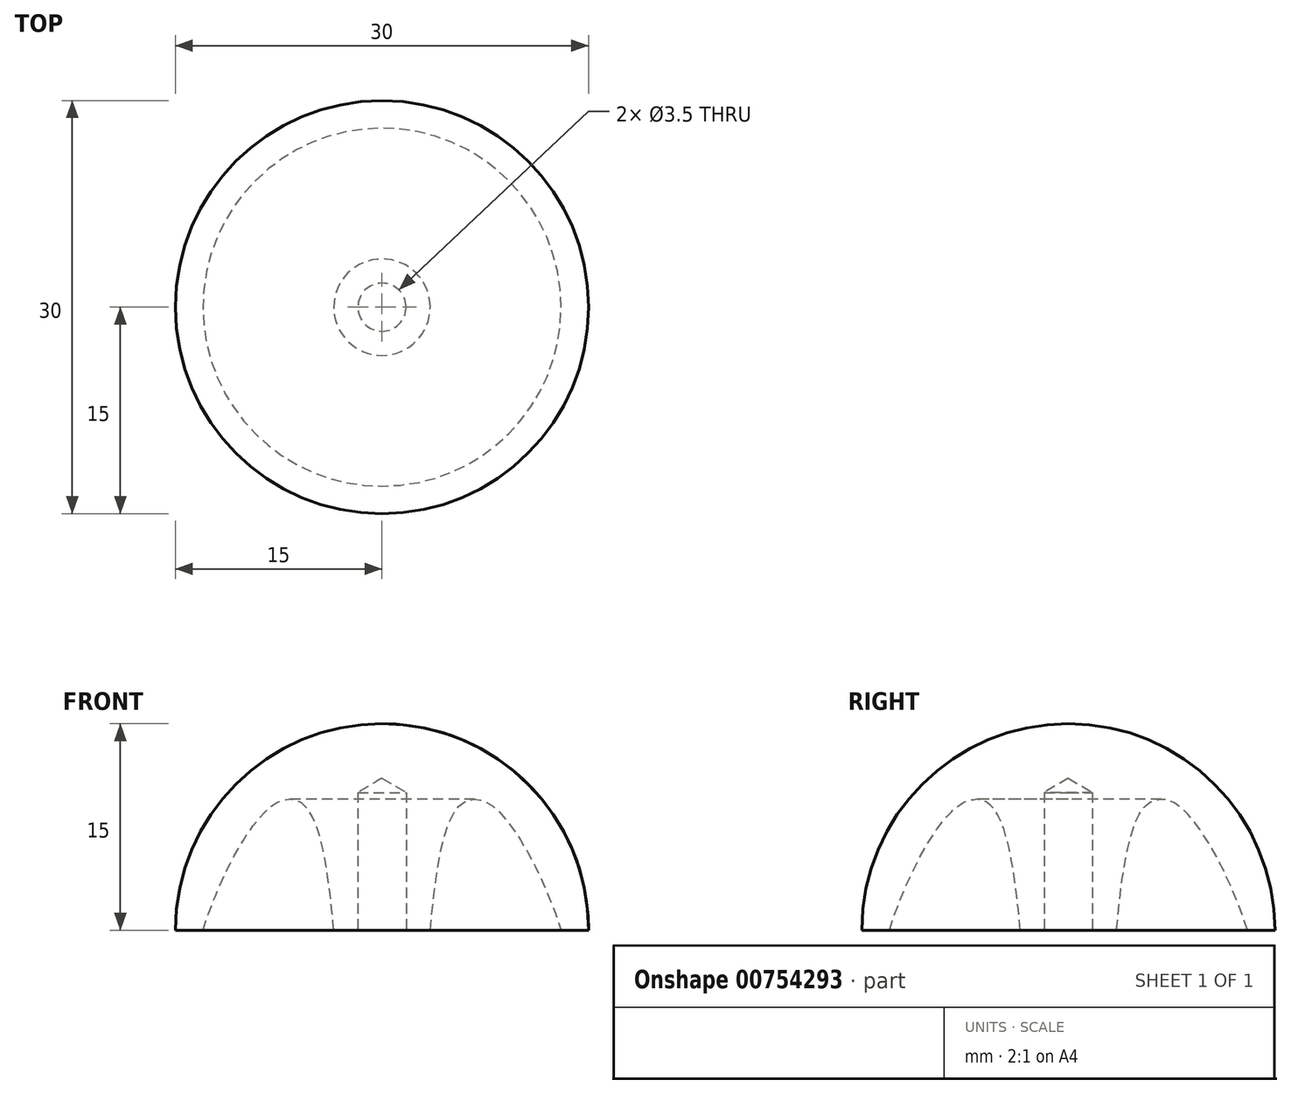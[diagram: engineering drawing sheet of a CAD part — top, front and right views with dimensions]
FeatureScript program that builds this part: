
annotation { "Feature Type Name" : "Feature", "Feature Type Description" : "" }
export const myFeature = defineFeature(function(context is Context, id is Id, definition is map)
    precondition{}
    {
        {
            var Q0;
            Q0=qCreatedBy(makeId("Front.planeOp"),FACE);
            var sketch = newSketch(context, id + "F0", { "sketchPlane" : qUnion([Q0])});
            skArc(sketch, "E0", {"start": v(15, 0) * mm, "mid": v(10.6, 10.6) * mm, "end": v(0, 15) * mm});
            skLineSegment(sketch, "E1", {"start": v(15, 0) * mm, "end": v(13, 0) * mm});
            skLineSegment(sketch, "E2", {"start": v(0, 0) * mm, "end": v(3.5, 0) * mm});
            skFitSpline(sketch, "E3", {"points": [v(3.5, 0) * mm, v(6.5, 9.48) * mm, v(8.26, 8.83) * mm, v(13, 0) * mm], "startDerivative": vector(4.9, 57.4) * mm, "endDerivative": vector(8.95, -28.49) * mm});
            skLineSegment(sketch, "E4", {"start": v(0, 15) * mm, "end": v(0, 0) * mm});
            skSolve(sketch);
        }
        {
            var Q0;
            Q0 = qSketchRegion(id + "F0", true);
            var Q1;
            Q1=sQuery(id+"F0.wireOp",EDGE,"E4");
            revolve(context, id + "F1", {"surfaceOperationType" : NewSurfaceOperationType.NEW, "entities" : qUnion([Q0]), "axis" : qUnion([Q1]), "revolveType" : RevolveType.FULL});
        }
        {
            var Q0;
            Q0=makeQuery(id+"F1.opRevolve","SWEPT_FACE",FACE,{"disambiguationData":[OSD([sQuery(id+"F0.wireOp",EDGE,"E2")])]});
            var sketch = newSketch(context, id + "F2", { "sketchPlane" : qUnion([Q0])});
            skPoint(sketch, "E5", {"position": v(0, 0) * mm});
            skSolve(sketch);
        }
        {
            var Q0;
            Q0=sQuery(id+"F2.wireOp",VERTEX,"E5");
            var Q1;
            Q1=makeQuery(id+"F1.opRevolve","SWEPT_BODY",BODY,{"disambiguationData":[OSD([sQuery(id+"F0.wireOp",EDGE,"E0"),sQuery(id+"F0.wireOp",EDGE,"E1"),sQuery(id+"F0.wireOp",EDGE,"E2"),sQuery(id+"F0.wireOp",EDGE,"E3"),sQuery(id+"F0.wireOp",EDGE,"E4")])]});
            hole(context, id + "F3", {"style" : HoleStyle.SIMPLE, "endStyle" : HoleEndStyle.BLIND, "holeDiameter" : 3.5 * mm, "majorDiameter" : 5 * mm, "holeDepth" : 10 * mm, "isTappedThrough" : true, "tappedDepth" : 12 * mm, "tapClearance" : 3, "locations" : qUnion([Q0]), "scope" : qUnion([Q1])});
        }
    });
